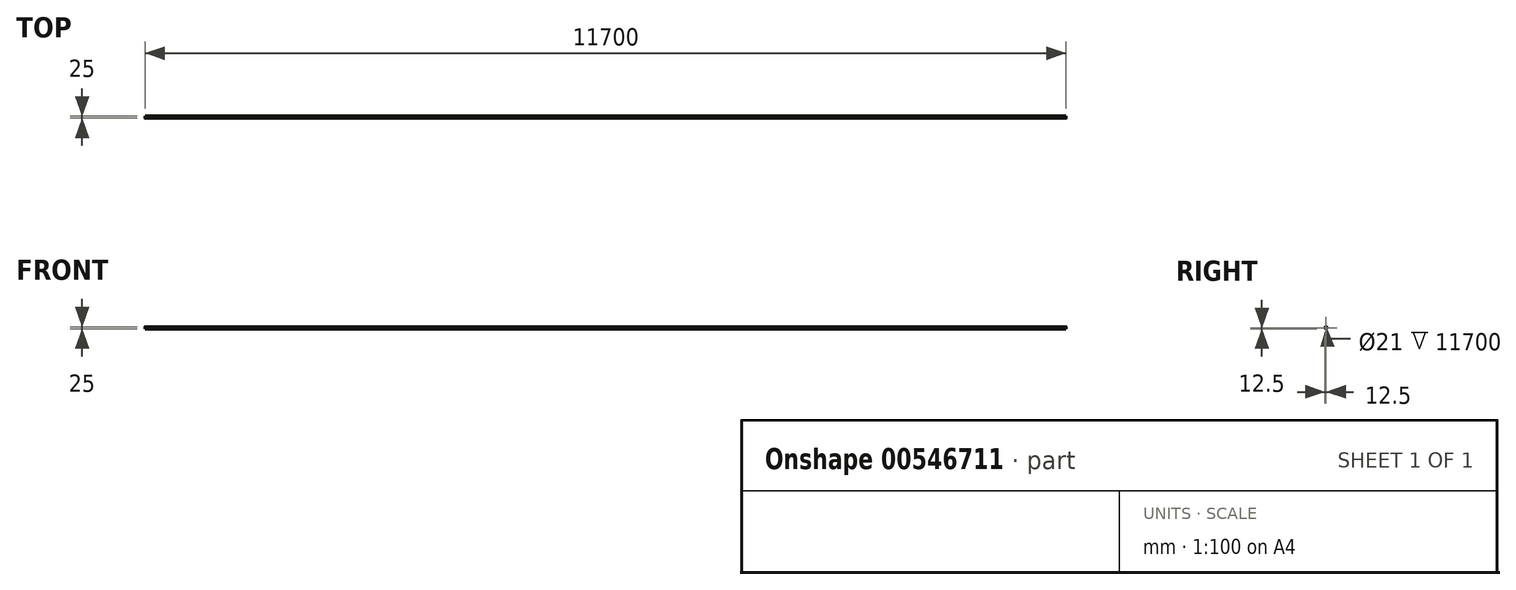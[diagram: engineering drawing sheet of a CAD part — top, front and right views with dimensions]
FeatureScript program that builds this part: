
annotation { "Feature Type Name" : "Feature", "Feature Type Description" : "" }
export const myFeature = defineFeature(function(context is Context, id is Id, definition is map)
    precondition{}
    {
        {
            var Q0;
            Q0=qCreatedBy(makeId("Right.planeOp"),FACE);
            var sketch = newSketch(context, id + "F0", { "sketchPlane" : qUnion([Q0])});
            skCircle(sketch, "E0", {"center": v(0, 0) * mm, "radius": 12.5 * mm});
            skCircle(sketch, "E1", {"center": v(0, 0) * mm, "radius": 10.5 * mm});
            skSolve(sketch);
        }
        {
            var Q0;
            Q0=makeQuery(id+"F0.imprint","IMPRINT",FACE,{"disambiguationData":[TD([[makeQuery(id+"F0.imprint","IMPRINT",EDGE,{"derivedFrom":sQuery(id+"F0.wireOp",EDGE,"E0")}),1.0]])]});
            extrude(context, id + "F1", {"entities" : qUnion([Q0]), "depth" : 11700 * mm, "offsetDistance" : 25 * mm});
        }
    });
